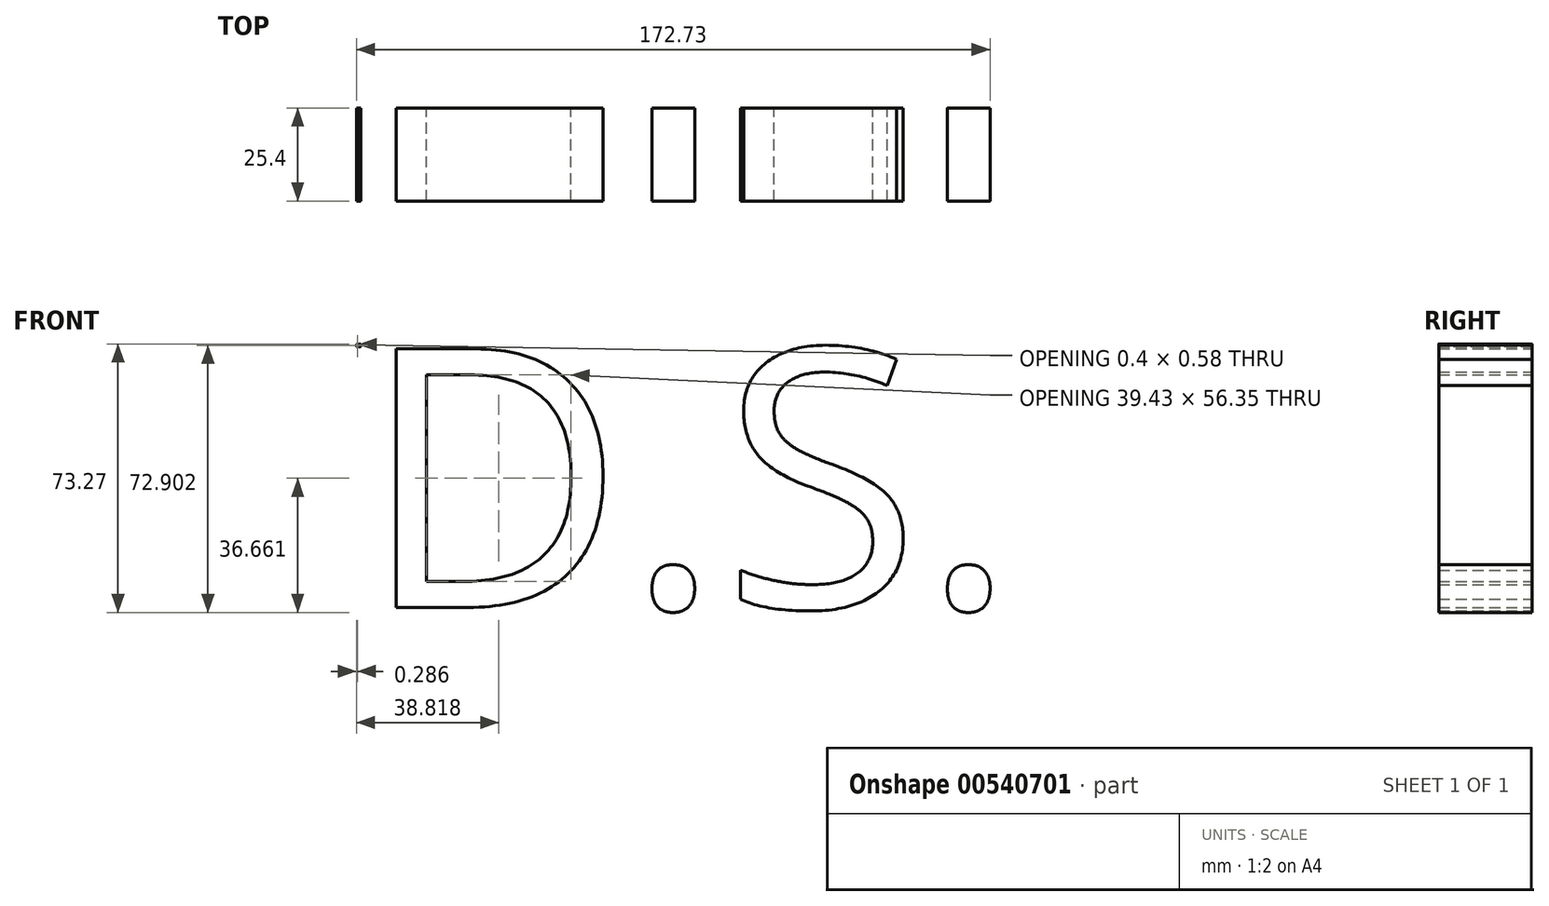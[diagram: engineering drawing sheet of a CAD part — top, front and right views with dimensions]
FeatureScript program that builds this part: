
annotation { "Feature Type Name" : "Feature", "Feature Type Description" : "" }
export const myFeature = defineFeature(function(context is Context, id is Id, definition is map)
    precondition{}
    {
        {
            var Q0;
            Q0=qCreatedBy(makeId("Front.planeOp"),FACE);
            var sketch = newSketch(context, id + "F0", { "sketchPlane" : qUnion([Q0])});
            skText(sketch, "E0", { "text": "DS", "fontName": "OpenSans-Regular.ttf"});
            skText(sketch, "E1", { "text": "D.S.", "fontName": "OpenSans-Regular.ttf"});
            const initialGuessF0  = {"E0": [-0.07171, 0.02187, 1, 0, 0.00073], "E1": [-0.0704, -0.04927, 1, 0, 0.07114]};
            skSetInitialGuess(sketch, initialGuessF0);
            skSolve(sketch);
        }
        {
            var Q0;
            Q0 = qSketchRegion(id + "F0", true);
            extrude(context, id + "F1", {"entities" : qUnion([Q0]), "depth" : 25.4 * mm, "offsetDistance" : 25.4 * mm});
        }
    });
